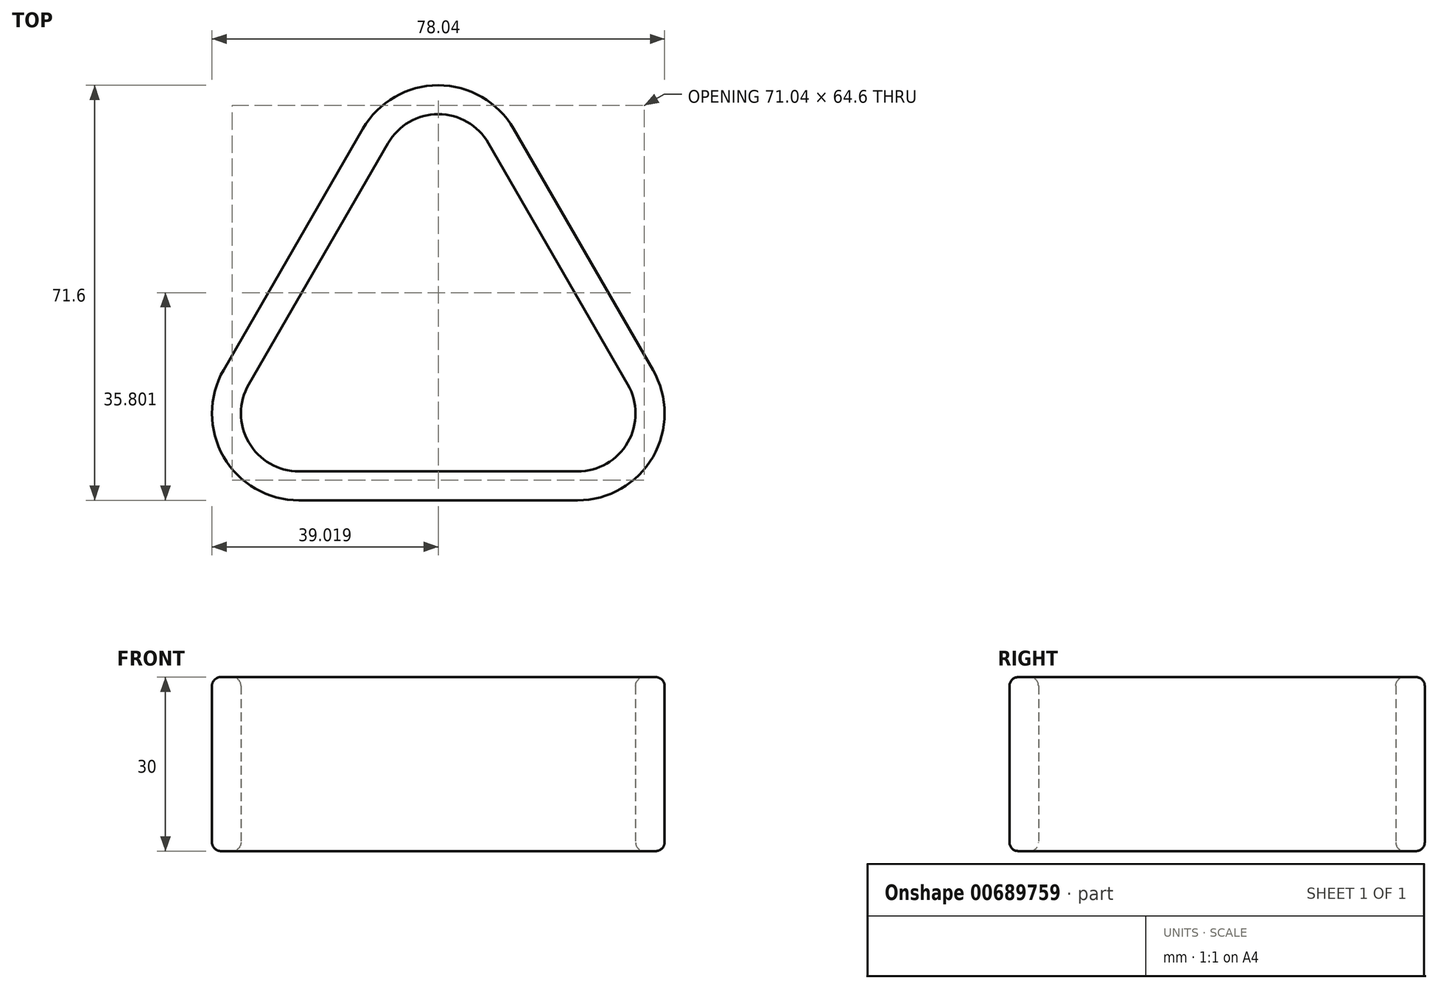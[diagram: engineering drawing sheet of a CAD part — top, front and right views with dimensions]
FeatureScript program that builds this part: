
annotation { "Feature Type Name" : "Feature", "Feature Type Description" : "" }
export const myFeature = defineFeature(function(context is Context, id is Id, definition is map)
    precondition{}
    {
        {
            var Q0;
            Q0=qCreatedBy(makeId("Top.planeOp"),FACE);
            var sketch = newSketch(context, id + "F0", { "sketchPlane" : qUnion([Q0])});
            skLineSegment(sketch, "E0", {"start": v(20, 0) * mm, "end": v(68.04, 0) * mm});
            skLineSegment(sketch, "E1", {"start": v(81.03, 22.5) * mm, "end": v(57, 64.1) * mm});
            skLineSegment(sketch, "E2", {"start": v(31.03, 64.1) * mm, "end": v(7, 22.5) * mm});
            skLineSegment(sketch, "E3.0", {"start": v(35.36, 61.6) * mm, "end": v(11.34, 20) * mm});
            skLineSegment(sketch, "E3.1", {"start": v(76.7, 20) * mm, "end": v(52.68, 61.6) * mm});
            skLineSegment(sketch, "E3.2", {"start": v(20, 5) * mm, "end": v(68.04, 5) * mm});
            skPoint(sketch, "E4.visualSharp", {"position": v(44.02, 76.6) * mm});
            skArc(sketch, "E4.filletArc", {"start": v(52.68, 61.6) * mm, "mid": v(44.02, 66.6) * mm, "end": v(35.36, 61.6) * mm});
            skPoint(sketch, "E5.visualSharp", {"position": v(85.36, 5) * mm});
            skArc(sketch, "E5.filletArc", {"start": v(68.04, 5) * mm, "mid": v(76.7, 10) * mm, "end": v(76.7, 20) * mm});
            skPoint(sketch, "E6.visualSharp", {"position": v(2.68, 5) * mm});
            skArc(sketch, "E6.filletArc", {"start": v(11.34, 20) * mm, "mid": v(11.34, 10) * mm, "end": v(20, 5) * mm});
            skArc(sketch, "E7.0", {"start": v(7, 22.5) * mm, "mid": v(7, 7.5) * mm, "end": v(20, 0) * mm});
            skArc(sketch, "E8.0", {"start": v(68.04, 0) * mm, "mid": v(81.03, 7.5) * mm, "end": v(81.03, 22.5) * mm});
            skArc(sketch, "E9.0", {"start": v(57, 64.1) * mm, "mid": v(44.02, 71.6) * mm, "end": v(31.03, 64.1) * mm});
            skSolve(sketch);
        }
        {
            var Q0;
            Q0=makeQuery(id+"F0.imprint","IMPRINT",FACE,{"disambiguationData":[TD([[makeQuery(id+"F0.imprint","IMPRINT",EDGE,{"derivedFrom":sQuery(id+"F0.wireOp",EDGE,"E0")}),1.0]])]});
            extrude(context, id + "F1", {"entities" : qUnion([Q0]), "depth" : 30 * mm, "offsetDistance" : 25 * mm});
        }
        {
            var Q0;
            Q0=makeQuery(id+"F1.opExtrude","SWEPT_FACE",FACE,{"disambiguationData":[OSD([sQuery(id+"F0.wireOp",EDGE,"E2")])]});
            var Q1;
            Q1=makeQuery(id+"F1.opExtrude","SWEPT_FACE",FACE,{"disambiguationData":[OSD([sQuery(id+"F0.wireOp",EDGE,"E3.0")])]});
            fillet(context, id + "F2", {"entities" : qUnion([Q0, Q1]), "radius" : 1.5 * mm, "tangentPropagation" : true, "allowEdgeOverflow" : false});
        }
    });
